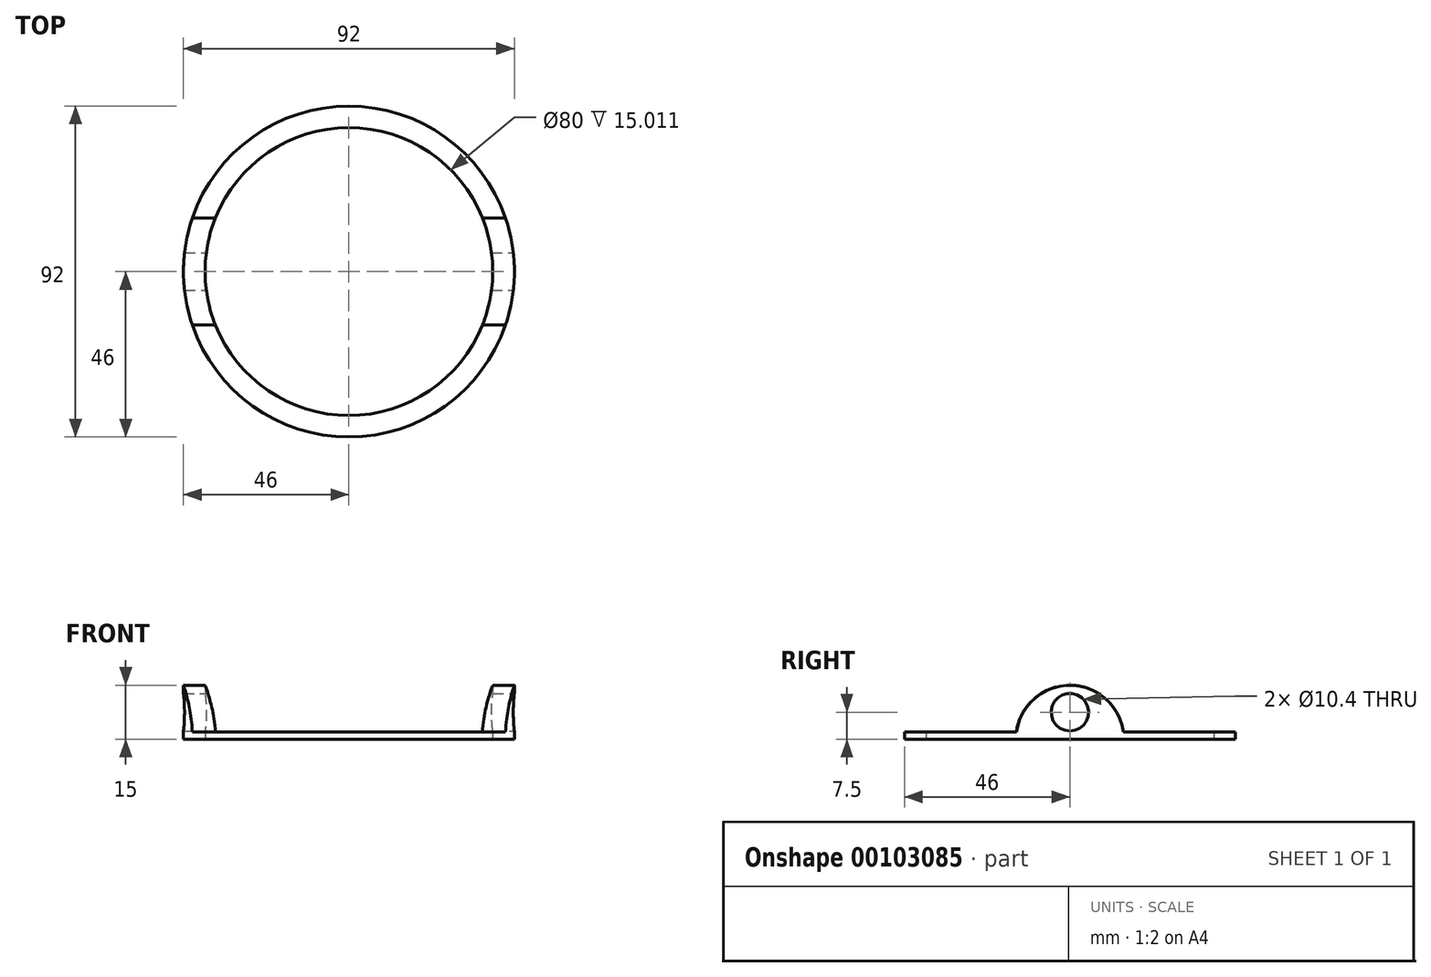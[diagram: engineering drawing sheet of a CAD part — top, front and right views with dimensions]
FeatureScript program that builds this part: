
annotation { "Feature Type Name" : "Feature", "Feature Type Description" : "" }
export const myFeature = defineFeature(function(context is Context, id is Id, definition is map)
    precondition{}
    {
        {
            var Q0;
            Q0=qCreatedBy(makeId("Top.planeOp"),FACE);
            var sketch = newSketch(context, id + "F0", { "sketchPlane" : qUnion([Q0])});
            skCircle(sketch, "E0", {"center": v(0, 0) * mm, "radius": 46 * mm});
            skCircle(sketch, "E1", {"center": v(0, 0) * mm, "radius": 40 * mm});
            skSolve(sketch);
        }
        {
            var Q0;
            Q0 = qSketchRegion(id + "F0", true);
            extrude(context, id + "F1", {"entities" : qUnion([Q0]), "depth" : 2 * mm});
        }
        {
            var Q0;
            Q0=qCreatedBy(makeId("Right.planeOp"),FACE);
            var sketch = newSketch(context, id + "F2", { "sketchPlane" : qUnion([Q0])});
            skLineSegment(sketch, "E2.0", {"start": v(-40, 0) * mm, "end": v(40, 0) * mm});
            skArc(sketch, "E3", {"start": v(-15, 0) * mm, "mid": v(0, -15) * mm, "end": v(15, 0) * mm, "construction": true});
            skArc(sketch, "E4", {"start": v(15, 0) * mm, "mid": v(0, 15) * mm, "end": v(-15, 0) * mm});
            skLineSegment(sketch, "E5", {"start": v(-15, 0) * mm, "end": v(15, 0) * mm});
            skSolve(sketch);
        }
        {
            var Q0;
            Q0 = qSketchRegion(id + "F2", true);
            var Q1;
            Q1 = qConstructionFilter(qBodyType(qCreatedBy(id + "F2" ,EDGE), BodyType.WIRE), ConstructionObject.NO);
            var Q2;
            Q2=makeQuery(id+"F1.opExtrude","SWEPT_FACE",FACE,{"disambiguationData":[OSD([sQuery(id+"F0.wireOp",EDGE,"E0")])]});
            var Q3;
            Q3=makeQuery(id+"F1.opExtrude","SWEPT_FACE",FACE,{"disambiguationData":[OSD([sQuery(id+"F0.wireOp",EDGE,"E0")])]});
            extrude(context, id + "F3", {"entities" : qUnion([Q0]), "operationType" : NewBodyOperationType.ADD, "surfaceEntities" : qUnion([Q1]), "endBound" : BoundingType.UP_TO_SURFACE, "endBoundEntityFace" : qUnion([Q2]), "depth" : 25 * mm, "hasSecondDirection" : true, "secondDirectionBound" : SecondDirectionBoundingType.UP_TO_SURFACE, "secondDirectionOppositeDirection" : true, "secondDirectionBoundEntityFace" : qUnion([Q3]), "secondDirectionDepth" : 25 * mm});
        }
        {
            var Q0;
            Q0=qCreatedBy(makeId("Top.planeOp"),FACE);
            var sketch = newSketch(context, id + "F4", { "sketchPlane" : qUnion([Q0])});
            skCircle(sketch, "E6.0", {"center": v(0, 0) * mm, "radius": 46 * mm});
            skCircle(sketch, "E7", {"center": v(0, 0) * mm, "radius": 51 * mm});
            skSolve(sketch);
        }
        {
            var Q0;
            Q0 = qSketchRegion(id + "F4", true);
            extrude(context, id + "F5", {"entities" : qUnion([Q0]), "operationType" : NewBodyOperationType.REMOVE, "endBound" : BoundingType.THROUGH_ALL, "depth" : 25 * mm});
        }
        {
            var Q0;
            Q0=qCreatedBy(makeId("Top.planeOp"),FACE);
            var sketch = newSketch(context, id + "F6", { "sketchPlane" : qUnion([Q0])});
            skCircle(sketch, "E8.0", {"center": v(0, 0) * mm, "radius": 40 * mm});
            skSolve(sketch);
        }
        {
            var Q0;
            Q0 = qSketchRegion(id + "F6", true);
            extrude(context, id + "F7", {"entities" : qUnion([Q0]), "operationType" : NewBodyOperationType.REMOVE, "endBound" : BoundingType.THROUGH_ALL, "depth" : 25 * mm});
        }
        {
            var Q0;
            Q0=qCreatedBy(makeId("Right.planeOp"),FACE);
            var sketch = newSketch(context, id + "F8", { "sketchPlane" : qUnion([Q0])});
            skArc(sketch, "E9.0", {"start": v(-14.87, 2) * mm, "mid": v(0, 15) * mm, "end": v(14.87, 2) * mm, "construction": true});
            skLineSegment(sketch, "E10.0", {"start": v(-40, 0) * mm, "end": v(40, 0) * mm});
            skLineSegment(sketch, "E11", {"start": v(0, 15) * mm, "end": v(0, 0) * mm, "construction": true});
            skCircle(sketch, "E12", {"center": v(0, 7.5) * mm, "radius": 5.2 * mm});
            skSolve(sketch);
        }
        {
            var Q0;
            Q0 = qSketchRegion(id + "F8", true);
            var Q1;
            Q1 = qConstructionFilter(qBodyType(qCreatedBy(id + "F8" ,EDGE), BodyType.WIRE), ConstructionObject.NO);
            extrude(context, id + "F9", {"entities" : qUnion([Q0]), "operationType" : NewBodyOperationType.REMOVE, "surfaceEntities" : qUnion([Q1]), "endBound" : BoundingType.THROUGH_ALL, "oppositeDirection" : true, "depth" : 25 * mm, "hasSecondDirection" : true, "secondDirectionBound" : SecondDirectionBoundingType.THROUGH_ALL, "secondDirectionOppositeDirection" : false, "secondDirectionDepth" : 25 * mm});
        }
    });
